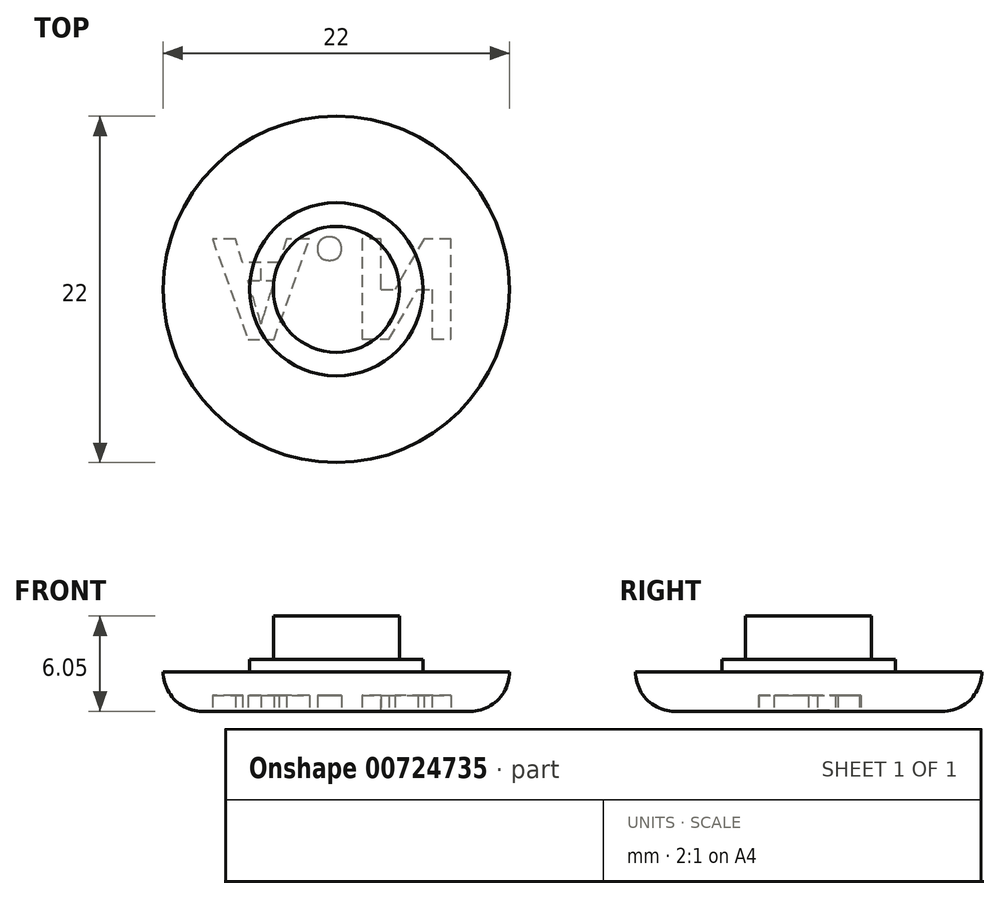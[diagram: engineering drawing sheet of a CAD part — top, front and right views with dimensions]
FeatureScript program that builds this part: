
annotation { "Feature Type Name" : "Feature", "Feature Type Description" : "" }
export const myFeature = defineFeature(function(context is Context, id is Id, definition is map)
    precondition{}
    {
        {
            var Q0;
            Q0=qCreatedBy(makeId("Top.planeOp"),FACE);
            var sketch = newSketch(context, id + "F0", { "sketchPlane" : qUnion([Q0])});
            skCircle(sketch, "E0", {"center": v(0, 0) * mm, "radius": 11 * mm});
            skCircle(sketch, "E1", {"center": v(0, 0) * mm, "radius": 4 * mm});
            skCircle(sketch, "E2", {"center": v(0, 0) * mm, "radius": 5.5 * mm});
            skSolve(sketch);
        }
        {
            var Q0;
            Q0=makeQuery(id+"F0.imprint","IMPRINT",FACE,{"disambiguationData":[TD([[makeQuery(id+"F0.imprint","IMPRINT",EDGE,{"derivedFrom":sQuery(id+"F0.wireOp",EDGE,"E0")}),1.0]])]});
            extrude(context, id + "F1", {"entities" : qUnion([Q0]), "depth" : 2.5 * mm, "offsetDistance" : 25 * mm});
        }
        {
            var Q0;
            Q0=makeQuery(id+"F0.imprint","IMPRINT",FACE,{"disambiguationData":[TD([[makeQuery(id+"F0.imprint","IMPRINT",EDGE,{"derivedFrom":sQuery(id+"F0.wireOp",EDGE,"E1")}),-1.0]])]});
            var Q1;
            Q1=makeQuery(id+"F1.opExtrude","CAP_FACE",FACE,{"disambiguationData":[OSD([sQuery(id+"F0.wireOp",EDGE,"E0"),sQuery(id+"F0.wireOp",EDGE,"E2")])],"isStart":false});
            extrude(context, id + "F2", {"entities" : qUnion([Q0]), "operationType" : NewBodyOperationType.ADD, "endBound" : BoundingType.UP_TO_SURFACE, "depth" : 25 * mm, "endBoundEntityFace" : qUnion([Q1]), "hasOffset" : true, "offsetDistance" : .8 * mm, "offsetOppositeDirection" : true});
        }
        {
            var Q0;
            Q0=makeQuery(id+"F0.imprint","IMPRINT",FACE,{"disambiguationData":[TD([[makeQuery(id+"F0.imprint","IMPRINT",EDGE,{"derivedFrom":sQuery(id+"F0.wireOp",EDGE,"E1")}),1.0]])]});
            var Q1;
            Q1=makeQuery(id+"F2.opExtrude","CAP_FACE",FACE,{"disambiguationData":[OSD([sQuery(id+"F0.wireOp",EDGE,"E0"),sQuery(id+"F0.wireOp",EDGE,"E2")])],"isStart":false});
            extrude(context, id + "F3", {"entities" : qUnion([Q0]), "operationType" : NewBodyOperationType.ADD, "endBound" : BoundingType.UP_TO_SURFACE, "depth" : 3 * mm, "endBoundEntityFace" : qUnion([Q1]), "hasOffset" : true, "offsetDistance" : 2.75 * mm, "offsetOppositeDirection" : true});
        }
        {
            var Q0;
            {var subQ0=sQuery(id+"F0.wireOp",EDGE,"E1");var subQ1=sQuery(id+"F0.wireOp",EDGE,"E2");Q0=makeQuery(id+"F3.boolean.opBoolean","MERGE",FACE,{"derivedFrom":[makeQuery(id+"F2.boolean.opBoolean","MERGE",FACE,{"derivedFrom":[makeQuery(id+"F1.opExtrude","CAP_FACE",FACE,{"disambiguationData":[OSD([sQuery(id+"F0.wireOp",EDGE,"E0"),subQ1])],"isStart":true}),makeQuery(id+"F2.opExtrude","CAP_FACE",FACE,{"disambiguationData":[OSD([subQ0,subQ1])],"isStart":true})]}),makeQuery(id+"F3.opExtrude","CAP_FACE",FACE,{"disambiguationData":[OSD([subQ0])],"isStart":true})]});}
            fillet(context, id + "F4", {"entities" : qUnion([Q0]), "radius" : 2.5 * mm, "tangentPropagation" : true, "allowEdgeOverflow" : false});
        }
        {
            var Q0;
            Q0=qCreatedBy(makeId("Right.planeOp"),FACE);
            var sketch = newSketch(context, id + "F5", { "sketchPlane" : qUnion([Q0])});
            skEllipse(sketch, "E3", {"center": v(-63.43, -1.89) * mm, "majorRadius": 11 * mm, "minorRadius": 2.5 * mm, "majorAxis": v(-1, 0)});
            skPoint(sketch, "E4", {"position": v(-63.43, 0.61) * mm});
            skLineSegment(sketch, "E5", {"start": v(-55.79, 0) * mm, "end": v(-71.08, 0) * mm});
            skArc(sketch, "E6", {"start": v(-11, 2.37) * mm, "mid": v(-6, 2.57) * mm, "end": v(-11, 2.5) * mm});
            skArc(sketch, "E7", {"start": v(6, 2.5) * mm, "mid": v(6, 2.46) * mm, "end": v(6, 2.42) * mm});
            skLineSegment(sketch, "E8", {"start": v(-63.43, 0.61) * mm, "end": v(-63.43, -4.39) * mm});
            skPoint(sketch, "E9.orphan", {"position": v(-63.43, -3.78) * mm});
            skPoint(sketch, "E10.orphan", {"position": v(-63.43, 0) * mm});
            skSolve(sketch);
        }
        {
            var Q0;
            {var subQ0=sQuery(id+"F0.wireOp",EDGE,"E1");var subQ1=sQuery(id+"F0.wireOp",EDGE,"E2");Q0=makeQuery(id+"F3.boolean.opBoolean","MERGE",FACE,{"derivedFrom":[makeQuery(id+"F2.boolean.opBoolean","MERGE",FACE,{"derivedFrom":[makeQuery(id+"F1.opExtrude","CAP_FACE",FACE,{"disambiguationData":[OSD([sQuery(id+"F0.wireOp",EDGE,"E0"),subQ1])],"isStart":true}),makeQuery(id+"F2.opExtrude","CAP_FACE",FACE,{"disambiguationData":[OSD([subQ0,subQ1])],"isStart":true})]}),makeQuery(id+"F3.opExtrude","CAP_FACE",FACE,{"disambiguationData":[OSD([subQ0])],"isStart":true})]});}
            var sketch = newSketch(context, id + "F6", { "sketchPlane" : qUnion([Q0])});
            skSolve(sketch);
        }
        {
            var Q0;
            {var subQ0=sQuery(id+"F0.wireOp",EDGE,"E1");var subQ1=sQuery(id+"F0.wireOp",EDGE,"E2");var subQ2=sQuery(id+"F0.wireOp",EDGE,"E0");Q0=makeQuery(id+"F6.imprint","IMPRINT",FACE,{"disambiguationData":[TD([[makeQuery(id+"F6.imprint","IMPRINT",EDGE,{"derivedFrom":makeQuery(id+"F4.opFillet","BLEND_EDGE",EDGE,{"blendedFrom":[makeQuery(id+"F1.opExtrude","CAP_EDGE",EDGE,{"disambiguationData":[OSD([subQ2])],"isStart":true}),makeQuery(id+"F3.boolean.opBoolean","MERGE",FACE,{"derivedFrom":[makeQuery(id+"F2.boolean.opBoolean","MERGE",FACE,{"derivedFrom":[makeQuery(id+"F1.opExtrude","CAP_FACE",FACE,{"disambiguationData":[OSD([subQ2,subQ1])],"isStart":true}),makeQuery(id+"F2.opExtrude","CAP_FACE",FACE,{"disambiguationData":[OSD([subQ0,subQ1])],"isStart":true})]}),makeQuery(id+"F3.opExtrude","CAP_FACE",FACE,{"disambiguationData":[OSD([subQ0])],"isStart":true})]})],"blendedInto":[makeQuery(id+"F3.boolean.opBoolean","MERGE",FACE,{"derivedFrom":[makeQuery(id+"F2.boolean.opBoolean","MERGE",FACE,{"derivedFrom":[makeQuery(id+"F1.opExtrude","CAP_FACE",FACE,{"disambiguationData":[OSD([subQ2,subQ1])],"isStart":true}),makeQuery(id+"F2.opExtrude","CAP_FACE",FACE,{"disambiguationData":[OSD([subQ0,subQ1])],"isStart":true})]}),makeQuery(id+"F3.opExtrude","CAP_FACE",FACE,{"disambiguationData":[OSD([subQ0])],"isStart":true})]})]})}),1.0]])]});}
            var sketch = newSketch(context, id + "F7", { "sketchPlane" : qUnion([Q0])});
            skLineSegment(sketch, "E11", {"start": v(-8.5, 0) * mm, "end": v(8.5, 0) * mm});
            skText(sketch, "E12", { "text": "A.N", "fontName": "OpenSans-Bold.ttf"});
            const initialGuessF7  = {"E12": [-0.00787, -0.00321, 1, 0, 0.00643]};
            skSetInitialGuess(sketch, initialGuessF7);
            skSolve(sketch);
        }
        {
            var Q0;
            Q0=qSketchRegion(id+"F7",true);
            extrude(context, id + "F8", {"entities" : qUnion([Q0]), "operationType" : NewBodyOperationType.REMOVE, "oppositeDirection" : true, "depth" : 1 * mm, "offsetDistance" : 25 * mm});
        }
        {
            var Q0;
            {var subQ0=sQuery(id+"F0.wireOp",EDGE,"E1");var subQ1=sQuery(id+"F0.wireOp",EDGE,"E2");var subQ2=sQuery(id+"F0.wireOp",EDGE,"E0");Q0=makeQuery(id+"F6.imprint","IMPRINT",FACE,{"disambiguationData":[TD([[makeQuery(id+"F6.imprint","IMPRINT",EDGE,{"derivedFrom":makeQuery(id+"F4.opFillet","BLEND_EDGE",EDGE,{"blendedFrom":[makeQuery(id+"F1.opExtrude","CAP_EDGE",EDGE,{"disambiguationData":[OSD([subQ2])],"isStart":true}),makeQuery(id+"F3.boolean.opBoolean","MERGE",FACE,{"derivedFrom":[makeQuery(id+"F2.boolean.opBoolean","MERGE",FACE,{"derivedFrom":[makeQuery(id+"F1.opExtrude","CAP_FACE",FACE,{"disambiguationData":[OSD([subQ2,subQ1])],"isStart":true}),makeQuery(id+"F2.opExtrude","CAP_FACE",FACE,{"disambiguationData":[OSD([subQ0,subQ1])],"isStart":true})]}),makeQuery(id+"F3.opExtrude","CAP_FACE",FACE,{"disambiguationData":[OSD([subQ0])],"isStart":true})]})],"blendedInto":[makeQuery(id+"F3.boolean.opBoolean","MERGE",FACE,{"derivedFrom":[makeQuery(id+"F2.boolean.opBoolean","MERGE",FACE,{"derivedFrom":[makeQuery(id+"F1.opExtrude","CAP_FACE",FACE,{"disambiguationData":[OSD([subQ2,subQ1])],"isStart":true}),makeQuery(id+"F2.opExtrude","CAP_FACE",FACE,{"disambiguationData":[OSD([subQ0,subQ1])],"isStart":true})]}),makeQuery(id+"F3.opExtrude","CAP_FACE",FACE,{"disambiguationData":[OSD([subQ0])],"isStart":true})]})]})}),1.0]])]});}
            var sketch = newSketch(context, id + "F9", { "sketchPlane" : qUnion([Q0])});
            skLineSegment(sketch, "E13.bottom", {"start": v(-4.79, -0.56) * mm, "end": v(-4.78, -0.56) * mm});
            skLineSegment(sketch, "E13.top", {"start": v(-4.79, -1.7) * mm, "end": v(-4.78, -1.7) * mm});
            skLineSegment(sketch, "E13.left", {"start": v(-4.79, -0.56) * mm, "end": v(-4.79, -1.7) * mm});
            skLineSegment(sketch, "E13.right", {"start": v(-4.78, -0.56) * mm, "end": v(-4.78, -1.7) * mm});
            skSolve(sketch);
        }
        {
            var Q0;
            Q0 = qSketchRegion(id + "F9", true);
            extrude(context, id + "F10", {"entities" : qUnion([Q0]), "operationType" : NewBodyOperationType.ADD, "oppositeDirection" : true, "depth" : .1 * mm, "offsetDistance" : 25 * mm});
        }
    });
